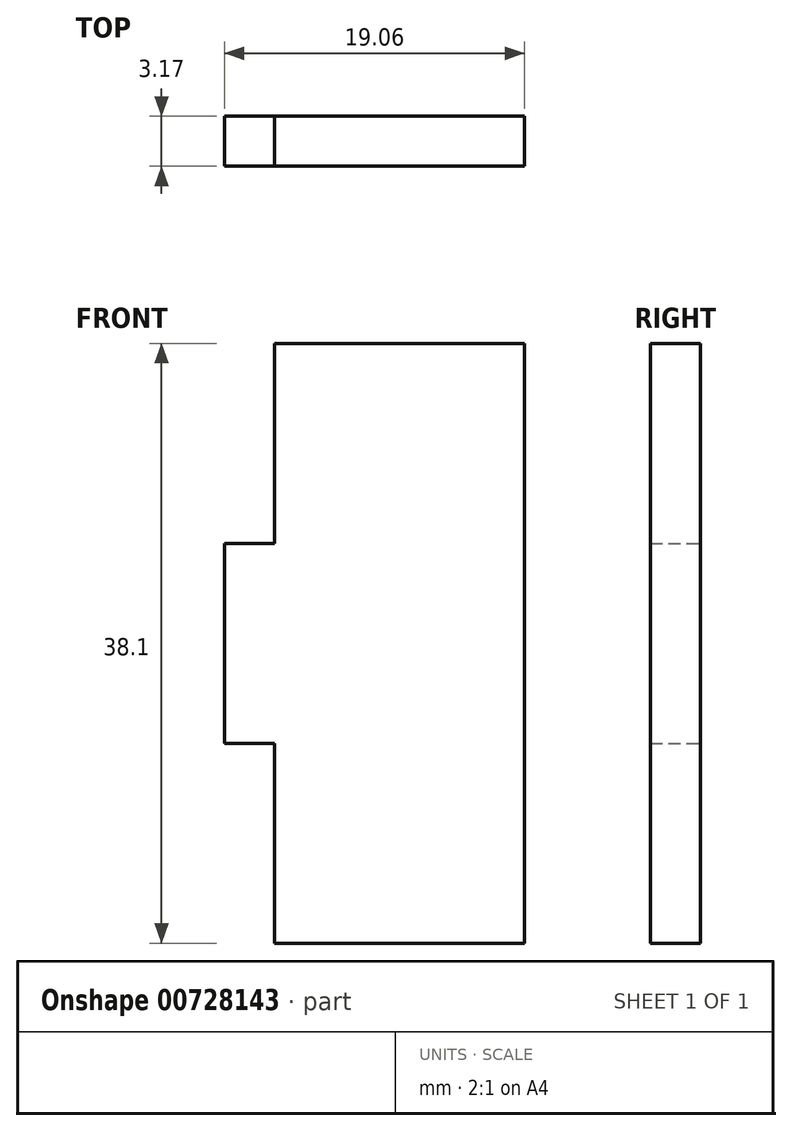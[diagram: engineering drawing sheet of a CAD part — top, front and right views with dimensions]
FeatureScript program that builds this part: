
annotation { "Feature Type Name" : "Feature", "Feature Type Description" : "" }
export const myFeature = defineFeature(function(context is Context, id is Id, definition is map)
    precondition{}
    {
        {
            var Q0;
            Q0=qCreatedBy(makeId("Front.planeOp"),FACE);
            var sketch = newSketch(context, id + "F0", { "sketchPlane" : qUnion([Q0])});
            skLineSegment(sketch, "E0.bottom", {"start": v(9.52, 31.75) * mm, "end": v(-9.53, 31.75) * mm});
            skLineSegment(sketch, "E0.top", {"start": v(9.52, -31.75) * mm, "end": v(-9.53, -31.75) * mm});
            skLineSegment(sketch, "E0.left", {"start": v(9.52, 31.75) * mm, "end": v(9.52, -31.75) * mm});
            skLineSegment(sketch, "E0.right", {"start": v(-9.53, 31.75) * mm, "end": v(-9.53, -31.75) * mm});
            skPoint(sketch, "E0.middle", {"position": v(0, 0) * mm});
            skLineSegment(sketch, "E1.bottom", {"start": v(-9.53, -31.75) * mm, "end": v(-6.35, -31.75) * mm});
            skLineSegment(sketch, "E1.top", {"start": v(-9.53, 31.75) * mm, "end": v(-6.35, 31.75) * mm});
            skLineSegment(sketch, "E1.left", {"start": v(-9.53, -31.75) * mm, "end": v(-9.53, 31.75) * mm});
            skLineSegment(sketch, "E1.right", {"start": v(-6.35, -31.75) * mm, "end": v(-6.35, 31.75) * mm});
            skLineSegment(sketch, "E2", {"start": v(-9.53, 19.05) * mm, "end": v(-6.35, 19.05) * mm});
            skLineSegment(sketch, "E3", {"start": v(-9.53, 6.35) * mm, "end": v(-6.35, 6.35) * mm});
            skLineSegment(sketch, "E4", {"start": v(-9.53, -6.35) * mm, "end": v(-6.35, -6.35) * mm});
            skLineSegment(sketch, "E5", {"start": v(-9.52, -19.05) * mm, "end": v(-6.35, -19.05) * mm});
            skLineSegment(sketch, "E6", {"start": v(-6.35, 19.05) * mm, "end": v(9.52, 19.05) * mm});
            skLineSegment(sketch, "E7", {"start": v(-6.35, -19.05) * mm, "end": v(9.52, -19.05) * mm});
            skSolve(sketch);
        }
        {
            var Q0;
            {var subQ0=sQuery(id+"F0.wireOp",EDGE,"E3");Q0=makeQuery(id+"F0.imprint","IMPRINT",FACE,{"disambiguationData":[TD([[makeQuery(id+"F0.imprint","IMPRINT",EDGE,{"derivedFrom":subQ0}),-1.0]])]});}
            var Q1;
            {var subQ0=sQuery(id+"F0.wireOp",EDGE,"E6");Q1=makeQuery(id+"F0.imprint","IMPRINT",FACE,{"disambiguationData":[TD([[makeQuery(id+"F0.imprint","IMPRINT",EDGE,{"derivedFrom":subQ0}),-1.0]])]});}
            extrude(context, id + "F1", {"entities" : qUnion([Q0, Q1]), "depth" : 3.17 * mm, "offsetDistance" : 25.4 * mm});
        }
    });
